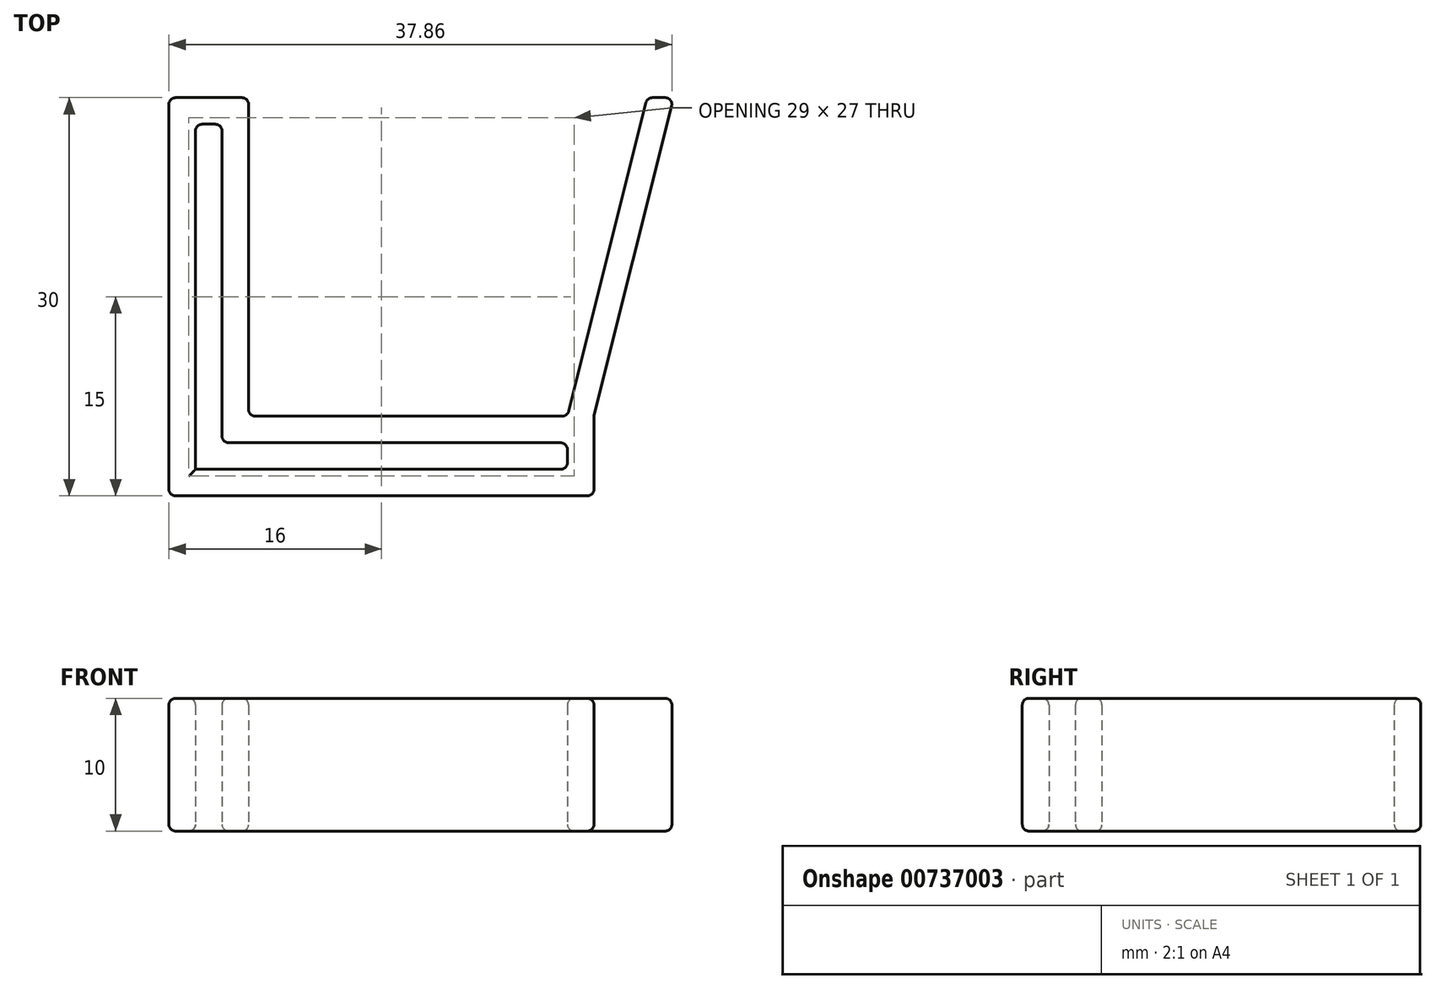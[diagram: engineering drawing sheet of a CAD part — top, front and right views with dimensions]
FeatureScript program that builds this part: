
annotation { "Feature Type Name" : "Feature", "Feature Type Description" : "" }
export const myFeature = defineFeature(function(context is Context, id is Id, definition is map)
    precondition{}
    {
        {
            var Q0;
            Q0=qCreatedBy(makeId("Top.planeOp"),FACE);
            var sketch = newSketch(context, id + "F0", { "sketchPlane" : qUnion([Q0])});
            skLineSegment(sketch, "E0", {"start": v(0, 0) * mm, "end": v(0, 24) * mm});
            skLineSegment(sketch, "E1", {"start": v(0, 0) * mm, "end": v(26, 0) * mm});
            skLineSegment(sketch, "E2", {"start": v(2, 2) * mm, "end": v(2, 26) * mm});
            skLineSegment(sketch, "E3", {"start": v(2, 26) * mm, "end": v(-4, 26) * mm});
            skLineSegment(sketch, "E4", {"start": v(-4, 26) * mm, "end": v(-4, 26) * mm});
            skLineSegment(sketch, "E5", {"start": v(-4, 26) * mm, "end": v(-4, -4) * mm});
            skLineSegment(sketch, "E6", {"start": v(0, 24) * mm, "end": v(-2, 24) * mm});
            skLineSegment(sketch, "E7", {"start": v(-2, 24) * mm, "end": v(-2, -2) * mm});
            skLineSegment(sketch, "E8", {"start": v(-2, -2) * mm, "end": v(26, -2) * mm});
            skLineSegment(sketch, "E9", {"start": v(26, -2) * mm, "end": v(26, 0) * mm});
            skLineSegment(sketch, "E10", {"start": v(28, -4) * mm, "end": v(-4, -4) * mm});
            skLineSegment(sketch, "E11", {"start": v(2, 2) * mm, "end": v(26, 2) * mm});
            skPoint(sketch, "E12", {"position": v(2, 2) * mm});
            skLineSegment(sketch, "E13", {"start": v(28, -4) * mm, "end": v(28, 2) * mm});
            skLineSegment(sketch, "E14", {"start": v(26, 2) * mm, "end": v(32, 26) * mm});
            skLineSegment(sketch, "E15", {"start": v(32, 26) * mm, "end": v(34, 26) * mm});
            skLineSegment(sketch, "E16", {"start": v(34, 26) * mm, "end": v(28, 2) * mm});
            skPoint(sketch, "E17.start.orphan", {"position": v(0, 0) * mm});
            skSolve(sketch);
        }
        {
            var Q0;
            Q0=makeQuery(id+"F0.imprint","IMPRINT",FACE,{"disambiguationData":[TD([[makeQuery(id+"F0.imprint","IMPRINT",EDGE,{"derivedFrom":sQuery(id+"F0.wireOp",EDGE,"E0")}),-1.0]])]});
            extrude(context, id + "F1", {"entities" : qUnion([Q0]), "depth" : 10 * mm, "offsetDistance" : 25 * mm});
        }
        {
            var Q0;
            Q0=makeQuery(id+"F1.opExtrude","CAP_FACE",FACE,{"disambiguationData":[OSD([sQuery(id+"F0.wireOp",EDGE,"E0"),sQuery(id+"F0.wireOp",EDGE,"E1"),sQuery(id+"F0.wireOp",EDGE,"E2"),sQuery(id+"F0.wireOp",EDGE,"E3"),sQuery(id+"F0.wireOp",EDGE,"E5"),sQuery(id+"F0.wireOp",EDGE,"E6"),sQuery(id+"F0.wireOp",EDGE,"E7"),sQuery(id+"F0.wireOp",EDGE,"E8"),sQuery(id+"F0.wireOp",EDGE,"E10"),sQuery(id+"F0.wireOp",EDGE,"E11"),sQuery(id+"F0.wireOp",EDGE,"E9"),sQuery(id+"F0.wireOp",EDGE,"E13"),sQuery(id+"F0.wireOp",EDGE,"E14"),sQuery(id+"F0.wireOp",EDGE,"E15"),sQuery(id+"F0.wireOp",EDGE,"E16")])],"isStart":false});
            var Q1;
            Q1=makeQuery(id+"F1.opExtrude","CAP_FACE",FACE,{"disambiguationData":[OSD([sQuery(id+"F0.wireOp",EDGE,"E0"),sQuery(id+"F0.wireOp",EDGE,"E1"),sQuery(id+"F0.wireOp",EDGE,"E2"),sQuery(id+"F0.wireOp",EDGE,"E3"),sQuery(id+"F0.wireOp",EDGE,"E5"),sQuery(id+"F0.wireOp",EDGE,"E6"),sQuery(id+"F0.wireOp",EDGE,"E7"),sQuery(id+"F0.wireOp",EDGE,"E8"),sQuery(id+"F0.wireOp",EDGE,"E10"),sQuery(id+"F0.wireOp",EDGE,"E11"),sQuery(id+"F0.wireOp",EDGE,"E9"),sQuery(id+"F0.wireOp",EDGE,"E13"),sQuery(id+"F0.wireOp",EDGE,"E14"),sQuery(id+"F0.wireOp",EDGE,"E15"),sQuery(id+"F0.wireOp",EDGE,"E16")])],"isStart":true});
            var Q2;
            Q2=makeQuery(id+"F1.opExtrude","SWEPT_FACE",FACE,{"disambiguationData":[OSD([sQuery(id+"F0.wireOp",EDGE,"E11")])]});
            var Q3;
            Q3=makeQuery(id+"F1.opExtrude","SWEPT_FACE",FACE,{"disambiguationData":[OSD([sQuery(id+"F0.wireOp",EDGE,"E3")])]});
            var Q4;
            Q4=makeQuery(id+"F1.opExtrude","SWEPT_EDGE",EDGE,{"disambiguationData":[OSD([sQuery(id+"F0.wireOp",EDGE,"E14"),sQuery(id+"F0.wireOp",EDGE,"E15")])]});
            var Q5;
            Q5=makeQuery(id+"F1.opExtrude","SWEPT_EDGE",EDGE,{"disambiguationData":[OSD([sQuery(id+"F0.wireOp",EDGE,"E15"),sQuery(id+"F0.wireOp",EDGE,"E16")])]});
            var Q6;
            Q6=makeQuery(id+"F1.opExtrude","SWEPT_FACE",FACE,{"disambiguationData":[OSD([sQuery(id+"F0.wireOp",EDGE,"E10")])]});
            var Q7;
            Q7=makeQuery(id+"F1.opExtrude","SWEPT_FACE",FACE,{"disambiguationData":[OSD([sQuery(id+"F0.wireOp",EDGE,"E16")])]});
            var Q8;
            Q8=makeQuery(id+"F1.opExtrude","SWEPT_FACE",FACE,{"disambiguationData":[OSD([sQuery(id+"F0.wireOp",EDGE,"E13")])]});
            var Q9;
            Q9=makeQuery(id+"F1.opExtrude","SWEPT_FACE",FACE,{"disambiguationData":[OSD([sQuery(id+"F0.wireOp",EDGE,"E0")])]});
            var Q10;
            Q10=makeQuery(id+"F1.opExtrude","SWEPT_FACE",FACE,{"disambiguationData":[OSD([sQuery(id+"F0.wireOp",EDGE,"E9")])]});
            var Q11;
            Q11=makeQuery(id+"F1.opExtrude","SWEPT_FACE",FACE,{"disambiguationData":[OSD([sQuery(id+"F0.wireOp",EDGE,"E6")])]});
            fillet(context, id + "F2", {"entities" : qUnion([Q0, Q1, Q2, Q3, Q4, Q5, Q6, Q7, Q8, Q9, Q10, Q11]), "radius" : 0.5 * mm, "tangentPropagation" : true, "allowEdgeOverflow" : false});
        }
    });
